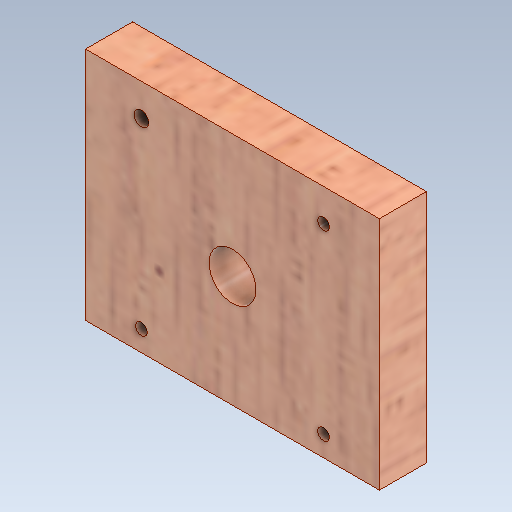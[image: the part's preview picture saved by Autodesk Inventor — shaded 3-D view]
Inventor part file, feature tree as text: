
AUTODESK INVENTOR PART (.ipt)
format: ipt  version: 2020 (Build 240168000, 168)  size: 250,880 bytes
history: native  units: mm
features: reference x4, other x3, extrude x2, sketch x2
ambient origin geometry x8: Origin, YZ Plane, XZ Plane, XY Plane, X Axis, Y Axis, Z Axis, Center Point
bodies: Solid1 (feature_tree)
feature tree (11):
  extrude  "Extrusion1"  Depth=40.0mm
  extrude  "Extrusion5"  Depth=8.0mm
  sketch  "Sketch1"  dims[d0=50.0mm d1=40.0mm]
  sketch  "Sketch5"  dims[d2=8.0mm d3=0.0mm d29=8.0mm d30=0.0mm d31=0.0mm]
  reference  "Reference1"
  reference  "Reference2"
  reference  "Reference3"
  reference  "Reference4"
  parser-record x1  (decoder bookkeeping rows leaked as tree rows — omitted from the tree; the rows remain in map.json)
  other  "0005-00-00 Ansamblu_General.iam"
  other  "0005-10-1001 NEMA17 - Motor de passo:4"
note: 1 file-system path scrubbed to <path> (originals preserved in map.json)
